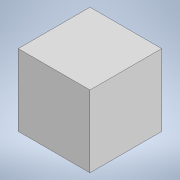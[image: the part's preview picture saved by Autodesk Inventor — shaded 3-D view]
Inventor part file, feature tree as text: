
AUTODESK INVENTOR PART (.ipt)
format: ipt  version: 2020.3 (Build 243373000, 373)  size: 83,968 bytes
history: native  units: mm
features: extrude x1, sketch x1
ambient origin geometry x8: Origin, YZ Plane, XZ Plane, XY Plane, X Axis, Y Axis, Z Axis, Center Point
bodies: Solid1 (feature_tree)
feature tree (2):
  extrude  "Extrusion1"  Depth=32.0mm
  sketch  "Sketch1"  dims[d0=32.0mm d1=32.0mm d2=32.0mm d3=0.0mm]
